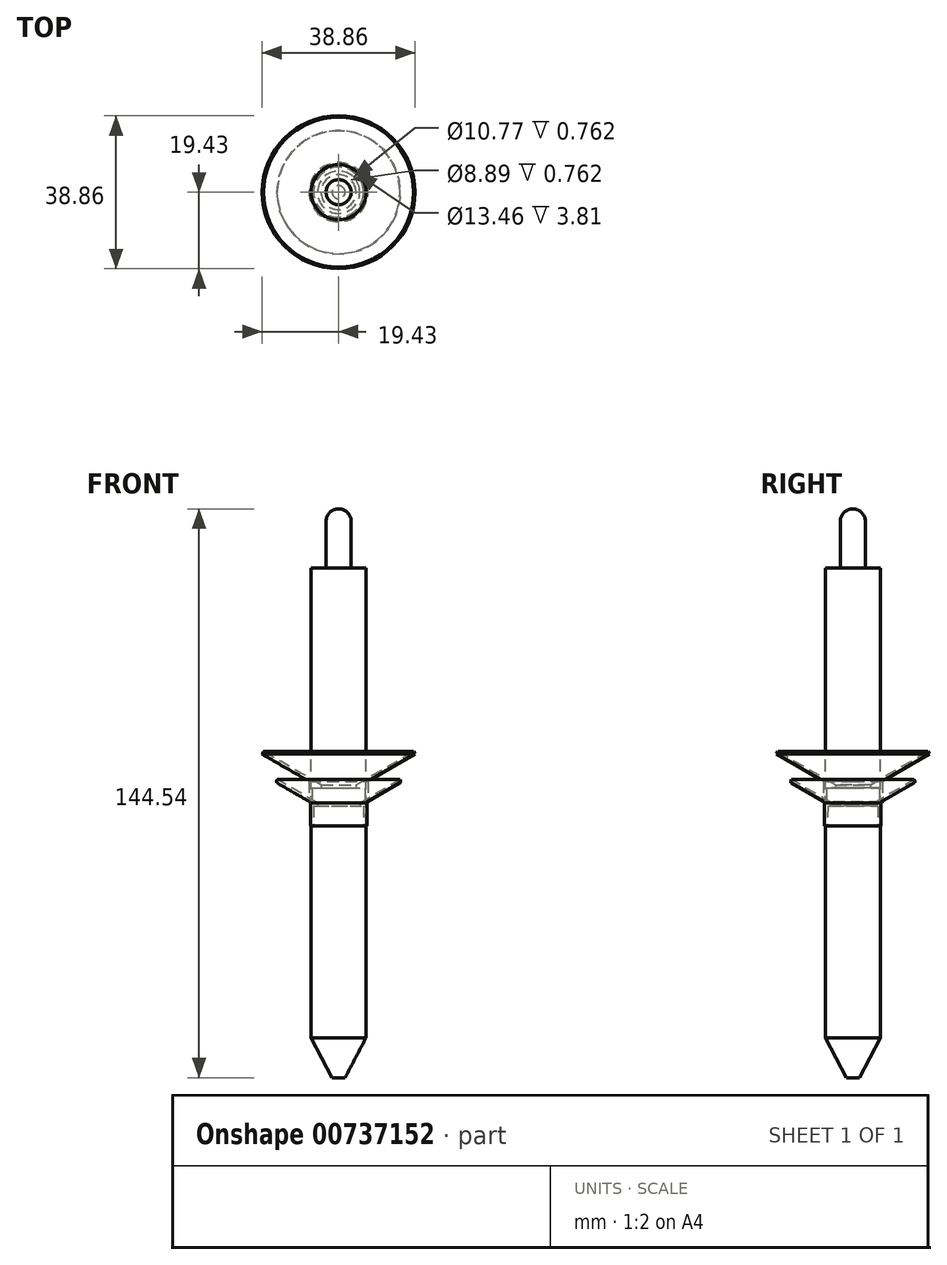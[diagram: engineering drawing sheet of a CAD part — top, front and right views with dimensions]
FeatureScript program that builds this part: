
annotation { "Feature Type Name" : "Feature", "Feature Type Description" : "" }
export const myFeature = defineFeature(function(context is Context, id is Id, definition is map)
    precondition{}
    {
        {
            var Q0;
            Q0=qCreatedBy(makeId("Front.planeOp"),FACE);
            var sketch = newSketch(context, id + "F0", { "sketchPlane" : qUnion([Q0])});
            skLineSegment(sketch, "E0", {"start": v(-4.44, 4.57) * mm, "end": v(-19.05, 13) * mm});
            skLineSegment(sketch, "E1", {"start": v(-19.05, 13) * mm, "end": v(-19.43, 12.34) * mm});
            skLineSegment(sketch, "E2", {"start": v(-19.43, 12.34) * mm, "end": v(-7.5, 5.45) * mm});
            skLineSegment(sketch, "E3", {"start": v(-7.5, 5.45) * mm, "end": v(-7.5, 0) * mm});
            skLineSegment(sketch, "E4", {"start": v(-7.5, 0) * mm, "end": v(-6.73, 0) * mm});
            skLineSegment(sketch, "E5", {"start": v(-4.44, 4.57) * mm, "end": v(-4.44, 3.81) * mm});
            skLineSegment(sketch, "E6", {"start": v(-4.44, 3.81) * mm, "end": v(-6.73, 3.8) * mm});
            skLineSegment(sketch, "E7", {"start": v(-6.73, 3.81) * mm, "end": v(-6.73, 0) * mm});
            skLineSegment(sketch, "E8", {"start": v(0, 0) * mm, "end": v(0, 20.24) * mm, "construction": true});
            skSolve(sketch);
        }
        {
            var Q0;
            Q0=makeQuery(id+"F0.imprint","IMPRINT",FACE,{"disambiguationData":[TD([[makeQuery(id+"F0.imprint","IMPRINT",EDGE,{"derivedFrom":sQuery(id+"F0.wireOp",EDGE,"E0")}),1.0]])]});
            var Q1;
            Q1=sQuery(id+"F0.wireOp",EDGE,"E8");
            revolve(context, id + "F1", {"surfaceOperationType" : NewSurfaceOperationType.NEW, "entities" : qUnion([Q0]), "axis" : qUnion([Q1]), "revolveType" : RevolveType.FULL});
        }
        {
            var Q0;
            Q0=qCreatedBy(makeId("Front.planeOp"),FACE);
            var sketch = newSketch(context, id + "F2", { "sketchPlane" : qUnion([Q0])});
            skLineSegment(sketch, "E9", {"start": v(0, 74.69) * mm, "end": v(0, -69.85) * mm});
            skLineSegment(sketch, "E10.top", {"start": v(-3.17, 59.7) * mm, "end": v(-6.98, 59.7) * mm});
            skLineSegment(sketch, "E10.right", {"start": v(-6.98, -59.7) * mm, "end": v(-6.98, 59.7) * mm});
            skLineSegment(sketch, "E11.bottom", {"start": v(0, 74.7) * mm, "end": v(-3.17, 74.7) * mm});
            skLineSegment(sketch, "E11.right", {"start": v(-3.17, 74.7) * mm, "end": v(-3.17, 59.7) * mm});
            skLineSegment(sketch, "E12", {"start": v(-6.98, -59.7) * mm, "end": v(-1.65, -69.85) * mm});
            skLineSegment(sketch, "E13", {"start": v(-1.65, -69.85) * mm, "end": v(0, -69.85) * mm});
            skLineSegment(sketch, "E14", {"start": v(-6.98, 0) * mm, "end": v(0, 0) * mm, "construction": true});
            skSolve(sketch);
        }
        {
            var Q0;
            Q0=makeQuery(id+"F2.imprint","IMPRINT",FACE,{"disambiguationData":[TD([[makeQuery(id+"F2.imprint","IMPRINT",EDGE,{"derivedFrom":sQuery(id+"F2.wireOp",EDGE,"E10.top")}),1.0]])]});
            var Q1;
            Q1=sQuery(id+"F2.wireOp",EDGE,"E9");
            revolve(context, id + "F3", {"surfaceOperationType" : NewSurfaceOperationType.NEW, "entities" : qUnion([Q0]), "axis" : qUnion([Q1]), "revolveType" : RevolveType.FULL});
        }
        {
            var Q0;
            Q0=makeQuery(id+"F3.opRevolve","SWEPT_EDGE",EDGE,{"disambiguationData":[OSD([sQuery(id+"F2.wireOp",EDGE,"E11.bottom"),sQuery(id+"F2.wireOp",EDGE,"E11.right")])]});
            fillet(context, id + "F4", {"entities" : qUnion([Q0]), "radius" : 3.17 * mm, "tangentPropagation" : true, "allowEdgeOverflow" : false});
        }
        {
            var Q0;
            Q0=qCreatedBy(makeId("Front.planeOp"),FACE);
            var sketch = newSketch(context, id + "F5", { "sketchPlane" : qUnion([Q0])});
            skLineSegment(sketch, "E15", {"start": v(0, -18.7) * mm, "end": v(0, 18.7) * mm, "construction": true});
            skLineSegment(sketch, "E16", {"start": v(-5.38, 0) * mm, "end": v(-15.58, 5.89) * mm});
            skLineSegment(sketch, "E17", {"start": v(-15.58, 5.89) * mm, "end": v(-15.96, 5.23) * mm});
            skLineSegment(sketch, "E18", {"start": v(-6.35, -0.76) * mm, "end": v(-5.38, -0.76) * mm});
            skLineSegment(sketch, "E19", {"start": v(-5.38, -0.76) * mm, "end": v(-5.38, 0) * mm});
            skLineSegment(sketch, "E20", {"start": v(-6.4, -5.84) * mm, "end": v(-7.16, -5.84) * mm});
            skLineSegment(sketch, "E21", {"start": v(-15.96, 5.23) * mm, "end": v(-7.16, 0.15) * mm});
            skLineSegment(sketch, "E22", {"start": v(-7.16, -5.84) * mm, "end": v(-7.16, 0.15) * mm});
            skLineSegment(sketch, "E23", {"start": v(-6.4, -5.84) * mm, "end": v(-6.35, -0.76) * mm});
            skSolve(sketch);
        }
        {
            var Q0;
            Q0=makeQuery(id+"F5.imprint","IMPRINT",FACE,{"disambiguationData":[TD([[makeQuery(id+"F5.imprint","IMPRINT",EDGE,{"derivedFrom":sQuery(id+"F5.wireOp",EDGE,"E16")}),1.0]])]});
            var Q1;
            Q1=sQuery(id+"F5.wireOp",EDGE,"E15");
            revolve(context, id + "F6", {"surfaceOperationType" : NewSurfaceOperationType.NEW, "entities" : qUnion([Q0]), "axis" : qUnion([Q1]), "revolveType" : RevolveType.FULL});
        }
        {
            var Q0;
            Q0=makeQuery(id+"F6.opRevolve","SWEPT_EDGE",EDGE,{"disambiguationData":[OSD([sQuery(id+"F5.wireOp",EDGE,"E17"),sQuery(id+"F5.wireOp",EDGE,"E21")])]});
            fillet(context, id + "F7", {"entities" : qUnion([Q0]), "radius" : 0.5 * mm, "tangentPropagation" : true, "allowEdgeOverflow" : false});
        }
    });
